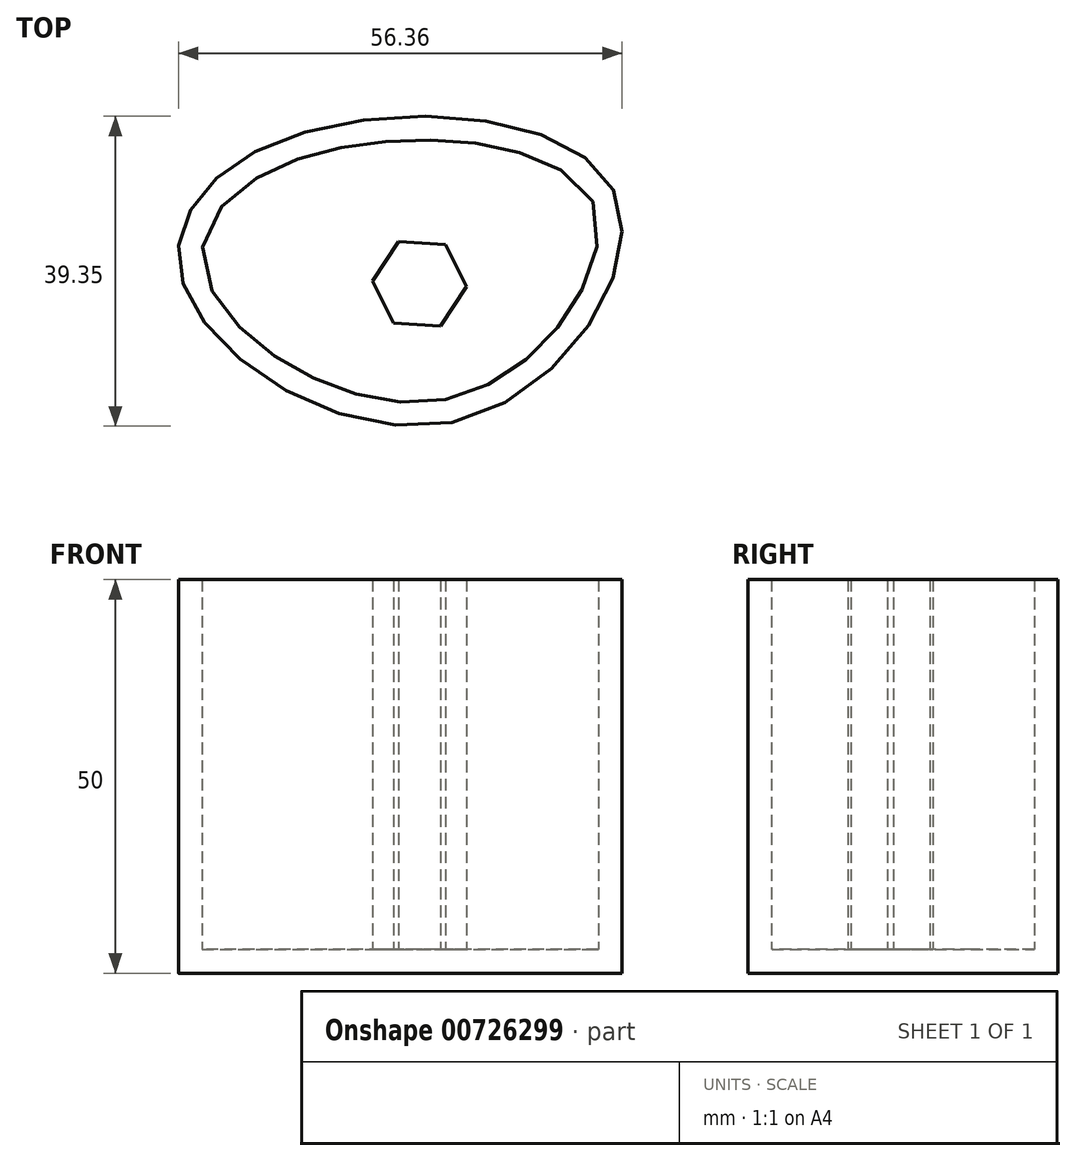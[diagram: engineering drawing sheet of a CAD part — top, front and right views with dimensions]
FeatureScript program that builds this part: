
annotation { "Feature Type Name" : "Feature", "Feature Type Description" : "" }
export const myFeature = defineFeature(function(context is Context, id is Id, definition is map)
    precondition{}
    {
        {
            var Q0;
            Q0=qCreatedBy(makeId("Top.planeOp"),FACE);
            var sketch = newSketch(context, id + "F0", { "sketchPlane" : qUnion([Q0])});
            skFitSpline(sketch, "E0", {"points": [v(-30, 0) * mm, v(-16.53, 18.63) * mm, v(24.74, 11.68) * mm, v(5.16, -17.37) * mm, v(-30, 0) * mm]});
            skSolve(sketch);
        }
        {
            var Q0;
            Q0 = qSketchRegion(id + "F0", true);
            extrude(context, id + "F1", {"entities" : qUnion([Q0]), "depth" : 50 * mm, "offsetDistance" : 25 * mm});
        }
        {
            var Q0;
            Q0=makeQuery(id+"F1.opExtrude","CAP_FACE",FACE,{"disambiguationData":[OSD([sQuery(id+"F0.wireOp",EDGE,"E0")])],"isStart":false});
            shell(context, id + "F2", {"entities" : qUnion([Q0]), "thickness" : 3 * mm});
        }
        {
            var Q0;
            Q0=makeQuery(id+"F1.opExtrude","CAP_FACE",FACE,{"disambiguationData":[OSD([sQuery(id+"F0.wireOp",EDGE,"E0")])],"isStart":false});
            var sketch = newSketch(context, id + "F3", { "sketchPlane" : qUnion([Q0])});
            skCircle(sketch, "E1.cCircle", {"center": v(0, 0) * mm, "radius": 5.2 * mm, "construction": true});
            skLineSegment(sketch, "E1.0", {"start": v(5.99, -0.37) * mm, "end": v(2.67, -5.37) * mm});
            skLineSegment(sketch, "E1.1", {"start": v(2.67, -5.37) * mm, "end": v(-3.32, -5) * mm});
            skLineSegment(sketch, "E1.2", {"start": v(-3.32, -5) * mm, "end": v(-5.99, 0.37) * mm});
            skLineSegment(sketch, "E1.3", {"start": v(-5.99, 0.37) * mm, "end": v(-2.67, 5.37) * mm});
            skLineSegment(sketch, "E1.4", {"start": v(-2.67, 5.37) * mm, "end": v(3.32, 5) * mm});
            skLineSegment(sketch, "E1.5", {"start": v(3.32, 5) * mm, "end": v(5.99, -0.37) * mm});
            skPoint(sketch, "E1.0.midPoint", {"position": v(4.33, -2.87) * mm});
            skSolve(sketch);
        }
        {
            var Q0;
            Q0=qCreatedBy(makeId("Front.planeOp"),FACE);
            var sketch = newSketch(context, id + "F4", { "sketchPlane" : qUnion([Q0])});
            skLineSegment(sketch, "E2", {"start": v(0, 50) * mm, "end": v(0, 3) * mm});
            skSolve(sketch);
        }
        {
            var Q0;
            Q0 = qSketchRegion(id + "F3", true);
            var Q1;
            Q1 = qConstructionFilter(qBodyType(qCreatedBy(id + "F4" ,EDGE), BodyType.WIRE), ConstructionObject.NO);
            sweep(context, id + "F5", {"profiles" : qUnion([Q0]), "path" : qUnion([Q1])});
        }
    });
